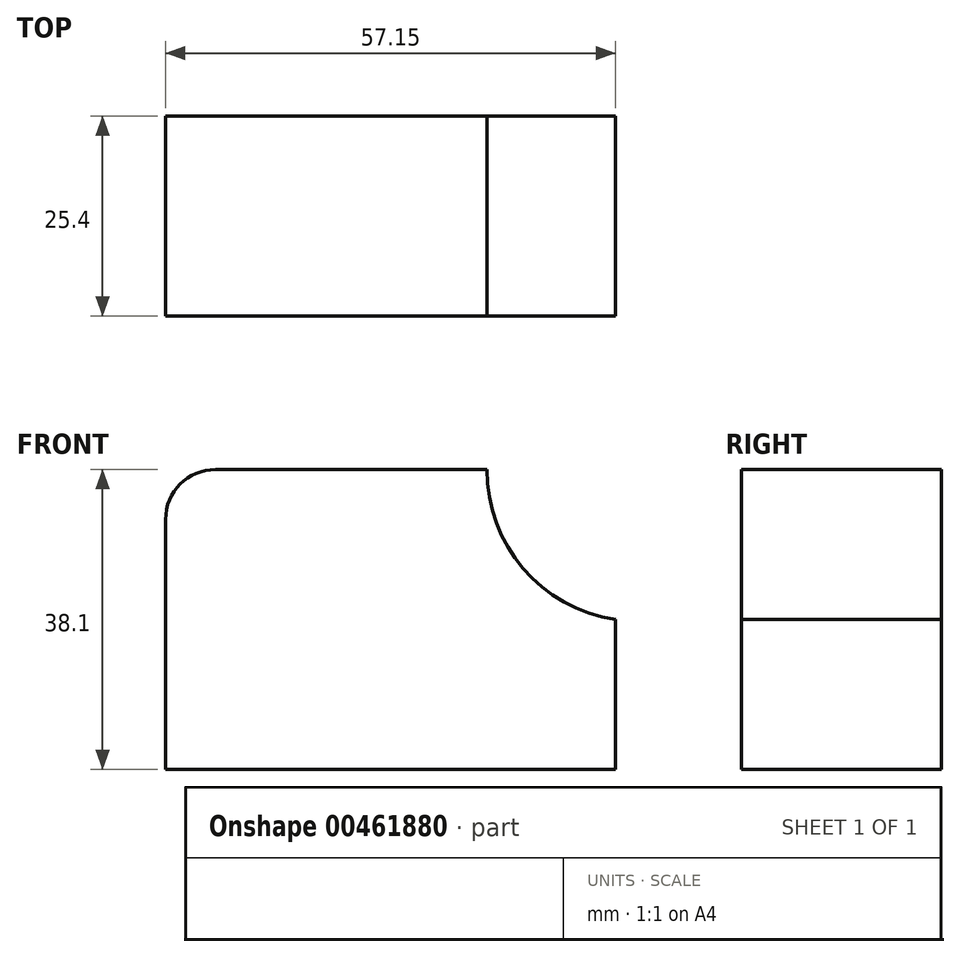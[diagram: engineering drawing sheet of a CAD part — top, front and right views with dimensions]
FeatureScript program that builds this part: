
annotation { "Feature Type Name" : "Feature", "Feature Type Description" : "" }
export const myFeature = defineFeature(function(context is Context, id is Id, definition is map)
    precondition{}
    {
        {
            var Q0;
            Q0=qCreatedBy(makeId("Front.planeOp"),FACE);
            var sketch = newSketch(context, id + "F0", { "sketchPlane" : qUnion([Q0])});
            skLineSegment(sketch, "E0.bottom", {"start": v(0, 0) * mm, "end": v(57.15, 0) * mm});
            skLineSegment(sketch, "E0.top", {"start": v(6.35, 38.1) * mm, "end": v(57.15, 38.1) * mm});
            skLineSegment(sketch, "E0.left", {"start": v(0, 0) * mm, "end": v(0, 31.75) * mm});
            skLineSegment(sketch, "E0.right", {"start": v(57.15, 0) * mm, "end": v(57.15, 38.1) * mm});
            skPoint(sketch, "E1.visualSharp", {"position": v(0, 38.1) * mm});
            skArc(sketch, "E1.filletArc", {"start": v(6.35, 38.1) * mm, "mid": v(1.86, 36.24) * mm, "end": v(0, 31.75) * mm});
            skArc(sketch, "E2", {"start": v(40.86, 38.1) * mm, "mid": v(45.43, 25.52) * mm, "end": v(57.15, 19.05) * mm});
            skSolve(sketch);
        }
        {
            var Q0;
            {var subQ1=sQuery(id+"F0.wireOp",EDGE,"E0.bottom");Q0=makeQuery(id+"F0.imprint","IMPRINT",FACE,{"disambiguationData":[TD([[makeQuery(id+"F0.imprint","IMPRINT",EDGE,{"derivedFrom":subQ1}),1.0]])]});}
            extrude(context, id + "F1", {"entities" : qUnion([Q0]), "depth" : 25.4 * mm});
        }
    });
